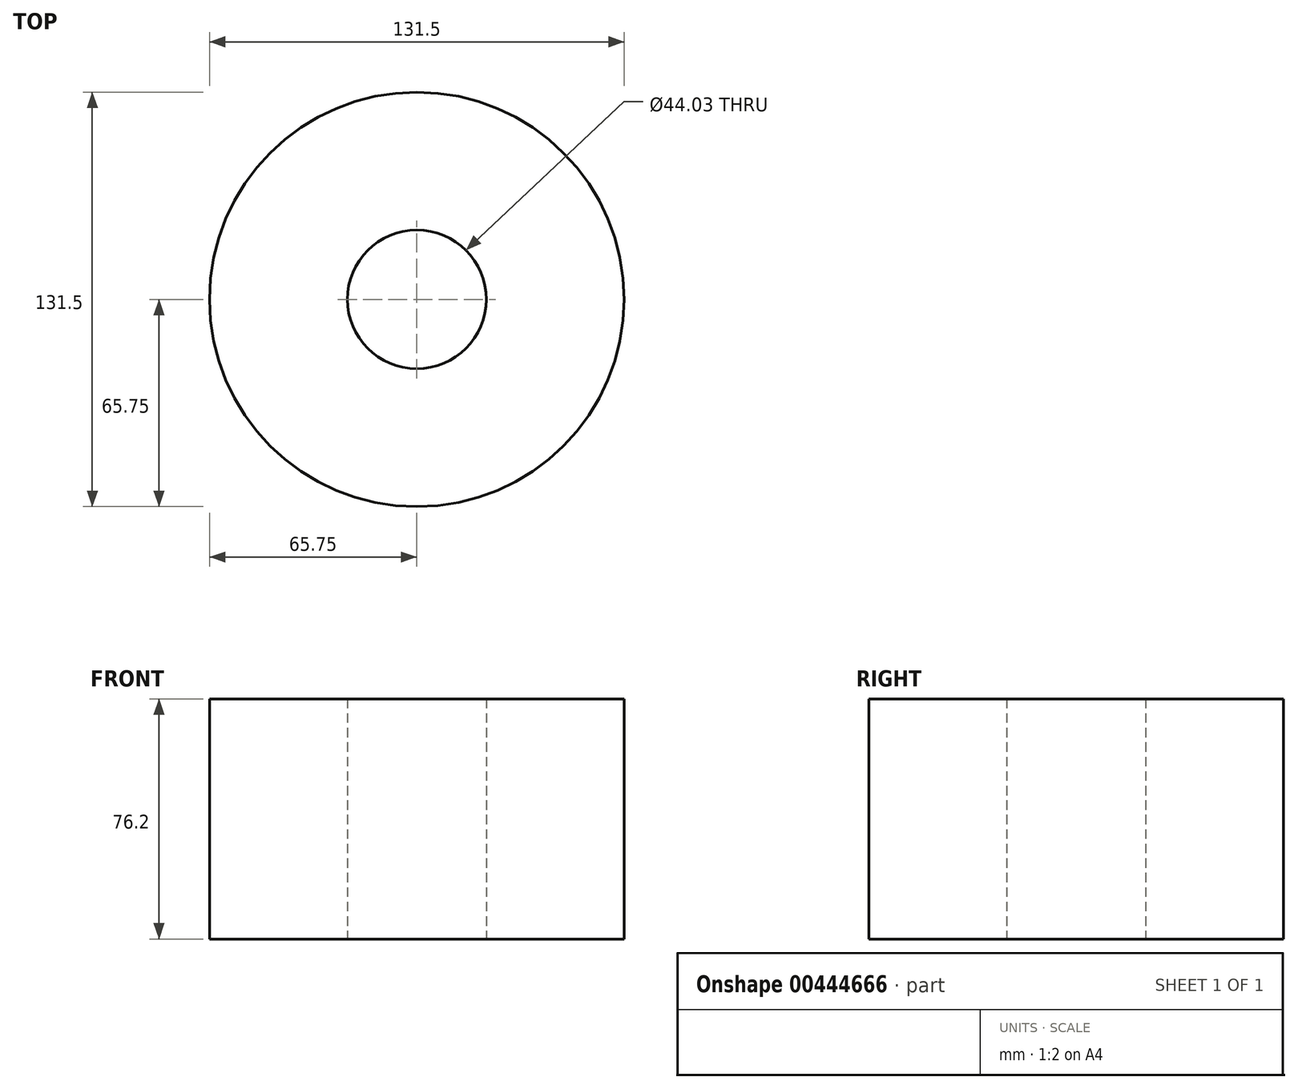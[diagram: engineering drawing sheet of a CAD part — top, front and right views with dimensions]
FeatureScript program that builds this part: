
annotation { "Feature Type Name" : "Feature", "Feature Type Description" : "" }
export const myFeature = defineFeature(function(context is Context, id is Id, definition is map)
    precondition{}
    {
        {
            var Q0;
            Q0=qCreatedBy(makeId("Top.planeOp"),FACE);
            var sketch = newSketch(context, id + "F0", { "sketchPlane" : qUnion([Q0])});
            skCircle(sketch, "E0", {"center": v(0, 0) * mm, "radius": 22.02 * mm});
            skCircle(sketch, "E1", {"center": v(0, 0) * mm, "radius": 65.75 * mm});
            skSolve(sketch);
        }
        {
            var Q0;
            Q0=makeQuery(id+"F0.imprint","IMPRINT",FACE,{"disambiguationData":[TD([[makeQuery(id+"F0.imprint","IMPRINT",EDGE,{"derivedFrom":sQuery(id+"F0.wireOp",EDGE,"E0")}),-1.0]])]});
            extrude(context, id + "F1", {"entities" : qUnion([Q0]), "depth" : 76.2 * mm});
        }
    });
